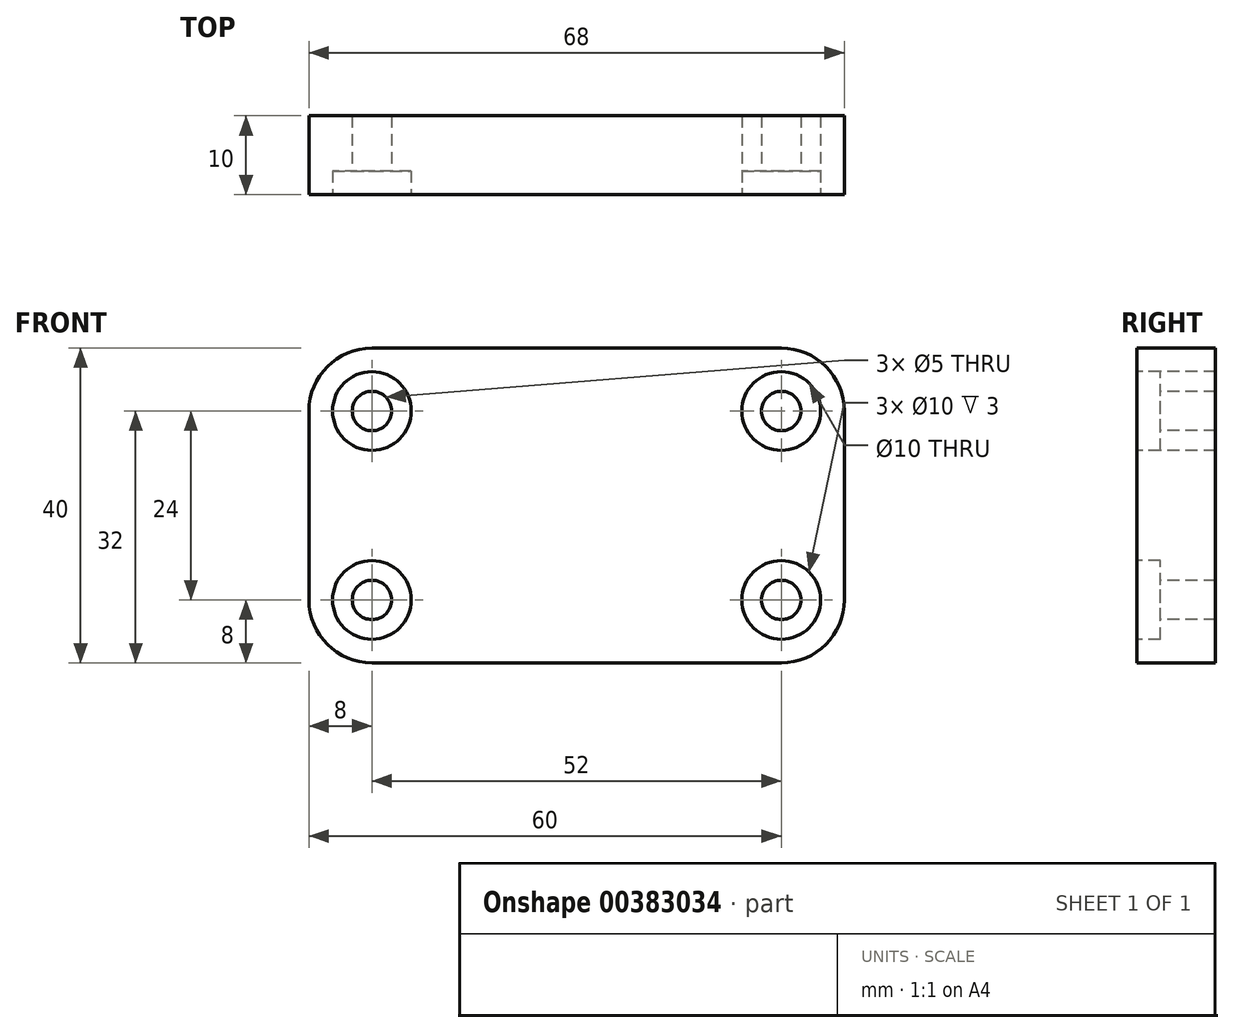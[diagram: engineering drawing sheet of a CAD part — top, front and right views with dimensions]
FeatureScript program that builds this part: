
annotation { "Feature Type Name" : "Feature", "Feature Type Description" : "" }
export const myFeature = defineFeature(function(context is Context, id is Id, definition is map)
    precondition{}
    {
        {
            var Q0;
            Q0=qCreatedBy(makeId("Front.planeOp"),FACE);
            var sketch = newSketch(context, id + "F0", { "sketchPlane" : qUnion([Q0])});
            skLineSegment(sketch, "E0.bottom", {"start": v(-26, 20) * mm, "end": v(26, 20) * mm});
            skLineSegment(sketch, "E0.top", {"start": v(-26, -20) * mm, "end": v(26, -20) * mm});
            skLineSegment(sketch, "E0.left", {"start": v(-34, 12) * mm, "end": v(-34, -12) * mm});
            skLineSegment(sketch, "E0.right", {"start": v(34, 12) * mm, "end": v(34, -12) * mm});
            skPoint(sketch, "E1.visualSharp", {"position": v(-34, 20) * mm});
            skArc(sketch, "E1.filletArc", {"start": v(-26, 20) * mm, "mid": v(-31.66, 17.66) * mm, "end": v(-34, 12) * mm});
            skPoint(sketch, "E2.visualSharp", {"position": v(34, 20) * mm});
            skArc(sketch, "E2.filletArc", {"start": v(34, 12) * mm, "mid": v(31.66, 17.66) * mm, "end": v(26, 20) * mm});
            skPoint(sketch, "E3.visualSharp", {"position": v(34, -20) * mm});
            skArc(sketch, "E3.filletArc", {"start": v(26, -20) * mm, "mid": v(31.66, -17.66) * mm, "end": v(34, -12) * mm});
            skPoint(sketch, "E4.visualSharp", {"position": v(-34, -20) * mm});
            skArc(sketch, "E4.filletArc", {"start": v(-34, -12) * mm, "mid": v(-31.66, -17.66) * mm, "end": v(-26, -20) * mm});
            skCircle(sketch, "E5", {"center": v(-26, 12) * mm, "radius": 5 * mm});
            skCircle(sketch, "E6", {"center": v(-26, -12) * mm, "radius": 5 * mm});
            skCircle(sketch, "E7", {"center": v(26, -12) * mm, "radius": 5 * mm});
            skCircle(sketch, "E8", {"center": v(-26, 12) * mm, "radius": 2.5 * mm});
            skCircle(sketch, "E9", {"center": v(26, -12) * mm, "radius": 2.5 * mm});
            skCircle(sketch, "E10", {"center": v(-26, -12) * mm, "radius": 2.5 * mm});
            skLineSegment(sketch, "E11", {"start": v(-14, -20) * mm, "end": v(-14, -12) * mm});
            skLineSegment(sketch, "E12", {"start": v(-14, -12) * mm, "end": v(14, -12) * mm});
            skLineSegment(sketch, "E13", {"start": v(14, -12) * mm, "end": v(14, -20) * mm});
            skCircle(sketch, "E14.MirrorC", {"center": v(26, 12) * mm, "radius": 2.5 * mm});
            skCircle(sketch, "E15.MirrorC", {"center": v(26, 12) * mm, "radius": 5 * mm});
            skLineSegment(sketch, "E16.MirrorCS", {"start": v(-14, 12) * mm, "end": v(14, 12) * mm});
            skLineSegment(sketch, "E17.MirrorCS", {"start": v(-14, 20) * mm, "end": v(-14, 12) * mm});
            skLineSegment(sketch, "E18.MirrorCS", {"start": v(14, 12) * mm, "end": v(14, 20) * mm});
            skSolve(sketch);
        }
        {
            var Q0;
            Q0=makeQuery(id+"F0.imprint","IMPRINT",FACE,{"disambiguationData":[TD([[makeQuery(id+"F0.imprint","IMPRINT",EDGE,{"derivedFrom":sQuery(id+"F0.wireOp",EDGE,"E0.left")}),1.0]])]});
            var Q1;
            Q1=makeQuery(id+"F0.imprint","IMPRINT",FACE,{"disambiguationData":[TD([[makeQuery(id+"F0.imprint","IMPRINT",EDGE,{"derivedFrom":sQuery(id+"F0.wireOp",EDGE,"E5")}),1.0]])]});
            var Q2;
            Q2=makeQuery(id+"F0.imprint","IMPRINT",FACE,{"disambiguationData":[TD([[makeQuery(id+"F0.imprint","IMPRINT",EDGE,{"derivedFrom":sQuery(id+"F0.wireOp",EDGE,"E14.MirrorC")}),1.0]])]});
            var Q3;
            Q3=makeQuery(id+"F0.imprint","IMPRINT",FACE,{"disambiguationData":[TD([[makeQuery(id+"F0.imprint","IMPRINT",EDGE,{"derivedFrom":sQuery(id+"F0.wireOp",EDGE,"E7")}),1.0]])]});
            var Q4;
            Q4=makeQuery(id+"F0.imprint","IMPRINT",FACE,{"disambiguationData":[TD([[makeQuery(id+"F0.imprint","IMPRINT",EDGE,{"derivedFrom":sQuery(id+"F0.wireOp",EDGE,"E6")}),1.0]])]});
            var Q5;
            {var subQ0=sQuery(id+"F0.wireOp",EDGE,"E11");Q5=makeQuery(id+"F0.imprint","IMPRINT",FACE,{"disambiguationData":[TD([[makeQuery(id+"F0.imprint","IMPRINT",EDGE,{"derivedFrom":subQ0}),-1.0]])]});}
            var Q6;
            Q6=makeQuery(id+"F0.imprint","IMPRINT",FACE,{"disambiguationData":[TD([[makeQuery(id+"F0.imprint","IMPRINT",EDGE,{"derivedFrom":sQuery(id+"F0.wireOp",EDGE,"E16.MirrorCS")}),1.0]])]});
            extrude(context, id + "F1", {"entities" : qUnion([Q0, Q1, Q2, Q3, Q4, Q5, Q6]), "oppositeDirection" : true, "depth" : 10 * mm});
        }
        {
            var Q0;
            Q0=makeQuery(id+"F0.imprint","IMPRINT",FACE,{"disambiguationData":[TD([[makeQuery(id+"F0.imprint","IMPRINT",EDGE,{"derivedFrom":sQuery(id+"F0.wireOp",EDGE,"E5")}),1.0]])]});
            var Q1;
            Q1=makeQuery(id+"F0.imprint","IMPRINT",FACE,{"disambiguationData":[TD([[makeQuery(id+"F0.imprint","IMPRINT",EDGE,{"derivedFrom":sQuery(id+"F0.wireOp",EDGE,"E14.MirrorC")}),1.0]])]});
            var Q2;
            Q2=makeQuery(id+"F0.imprint","IMPRINT",FACE,{"disambiguationData":[TD([[makeQuery(id+"F0.imprint","IMPRINT",EDGE,{"derivedFrom":sQuery(id+"F0.wireOp",EDGE,"E7")}),1.0]])]});
            var Q3;
            Q3=makeQuery(id+"F0.imprint","IMPRINT",FACE,{"disambiguationData":[TD([[makeQuery(id+"F0.imprint","IMPRINT",EDGE,{"derivedFrom":sQuery(id+"F0.wireOp",EDGE,"E6")}),1.0]])]});
            extrude(context, id + "F2", {"entities" : qUnion([Q0, Q1, Q2, Q3]), "operationType" : NewBodyOperationType.REMOVE, "oppositeDirection" : true, "depth" : 3 * mm});
        }
    });
